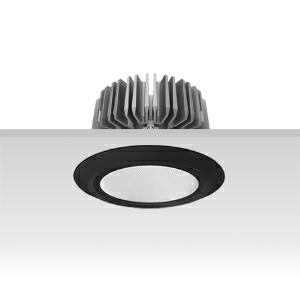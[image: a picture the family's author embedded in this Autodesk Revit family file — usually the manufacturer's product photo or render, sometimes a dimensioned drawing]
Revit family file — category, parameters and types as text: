
# Revit family: 3f_filippi_-_3f_reno_bianco_ampio_3f_filippi_-_30345_a01036_-_3f_reno_150_wh_2000-930_wide___vs_bk_4bb8
name_source: partatom
category: Lighting Fixtures
units: mm (PartAtom-declared; Revit-internal decimal feet)

## family parameters
Cut with Voids When Loaded = No
Host = Face
Light Source = No
Part Type = Normal
Room Calculation Point = No
Round Connector Dimension = Use Diameter
Shared = No

## types (1)
- 3F Filippi - 3F Reno Bianco Ampio (1 x LED, 1636 lm, 24 W, 3000 K)
    Apparent Load = 24 VA
    Approval mark = CE
    CIE Flux Codes = 74 93 99 100 100
    Color Rendering = 90
    Color Temperature = 3000 K
    Control Gear = Electronic ballast
    Default Elevation = 1800 mm
    Description = ILLUMINOTECHNICAL
Luminous efficiency 100% (DLOR 100%, ULOR 0%).
Initial luminous flux of the luminaire 1636 lm.
Direct symmetric wide distribution.
Installation Interdistance Transv.D = 1.12 x hu - Long.D = 1.11 x hu.
Tabular UGR (CIE 117 - 4H-8H; S=0.25H; 70/50/20): RUG 22.7 - 22.5.
Beam angle: 74° - 73°.
Luminous efficacy 68 lm/W.
Lifetime (L90/B10): 30000 h. (tq+25°C)
Lifetime (L85/B10): 50000 h. (tq+25°C)
Lifetime (L70/B10): 80000 h. (tq+25°C)
Sudden decreased luminous flux after 50000 hours: 0% (C0).
Photobiological safety in compliance with IEC/TR 62778: RG0 risk exempt, (IEC 62471).
In compliance with IEC/EN 62722-2-1 - IEC/EN 62717 standards.

SOURCE
Compact LED module 2000/930.
Energy efficiency class (UE 2019/2020 - UE 2019/2015): E.
CIE 13.3 Colour rendering index: CRI >90 (R9 >50%).
IES TM-30 Fidelity Index: Rf = 92 Rg = 101.
CCT nominal colour temperature 3000 K.
Colour initial tolerance (MacAdam): SDCM 3.
Zhaga Book 3 compliant.

MECHANICAL
Passive heat dissipator in die-casting aluminium, oversized, for optimum thermal management of the LED module.
Parabolic element with graduated/concentric rings in white polycarbonate.
Transparent external lens with glossy and satin differentiated surfaces, with a cooling and anti-insect system in methacrylate (PMMA).
Fastening spring clips in stainless steel.
Dimensions: diameter 176 mm, height 111 mm. Weight 0.81 kg.
IP44 protection degree for exposed part, IP20 for recessed part.
Mechanical strength to impacts IK06 (1 joule).
Glow-wire test resistance 650°C.

ELECTRICAL
Wiring on a separate unit.
Halogen Free electronic wiring 230V-50/60Hz, power factor 0.95, THD <25%, constant output current, SELV, class II, 1 driver.
Power of the luminaire 24 W.
ENEC - CE.
SAFE FLICKER: PstLM=<1 and SVM=<0.4 (IEC TR 61547-1 and IEC TR 63158), to ensure a more comfortable and safe light.
Luminaire compliant with EN 60598-2-22 for power supply from a centralised emergency system CPSS (Central Power Supply System), not incorporated in the luminaire - high risk areas excluded. The default power and flux are 100% in AC and 100% in DC.
Ambient temperature from 0°C to +25°C.
Temperature class T6 max 85°C.
Relative humidity UR: <85%.

INSTALLATION
Pull-up recessed fitting.
False ceiling carving: 150 mm.
All accessories dedicated to this product are available on the Catalog and on our website www.3F-Filippi.com.

ACCESSORIES
A01036 - Anti-glare microprismatic VS moulded glass, tempered, not flammable, locked and in line with the trim, in black polycarbonate.

APPLICATIONS
Environments: architectural, commercial, exhibition areas, transit areas, corridors, shops, display windows, service areas.
In false ceilings with narrow voids.

WARNING
Luminaire designed for disposal/recycling at end-of-life.
Replaceable (LED only) light source by a professional. Replaceable control gear by a professional.
    Height = 0 mm  [stored 0 ft]
    Lamp = 1 x LED
    Lamp Light Flux = 1636 lm
    Lamp Power = 24 W
    Lamp count = 1
    Length = 176 mm
    Lifetime = 50000 h
    Luminous efficacy = 68 lm/W
    Manufacturer = 3F Filippi
    ModVariant = No
    Model = 3F Filippi - 30345+A01036 - 3F Reno 150 WH 2000-930 WIDE + VS BK
    Mounting Place = Ceiling
    Mounting Type = Recessed
    Number of Poles = 1
    OnlyDefault = Yes
    Power Factor = 1
    Product Name = 3F Filippi - 3F Reno Bianco Ampio
    Product group = recessed luminaire
    ProductGroupID = 4
    Protection Class = Protection class II
    Protection Degree = IP 20
    RLX_Detail_Level = 1
    RLX_Emergency_Light_Flux = 0 lm
    RLX_Emergency_Type = 0
    RLX_Emergency_Type_DB = No
    RlxData = <blob elided: 85077 chars, md5=c0f9d932>
    Socket = socket
    Standby Power = 0 W
    System Light Flux = 1636 lm
    System Power = 24 W
    Type Comments = Product without accessories
    Type Image = 3ffilippi_3f_reno_150_bk_vs_smp.jpg
    URL = http://relux.com
    VarID = ---
    Voltage = 0 V
    Weight = 0.00 kg
    Width = 0 mm  [stored 0 ft]

note: [stored X ft] marks values corroborated as IEEE doubles in the binary element streams (Revit-internal decimal feet)

## geometry (parser evidence)
native form markers: Blend x4, Sweep x11
no freeform markers — native parametric forms only
